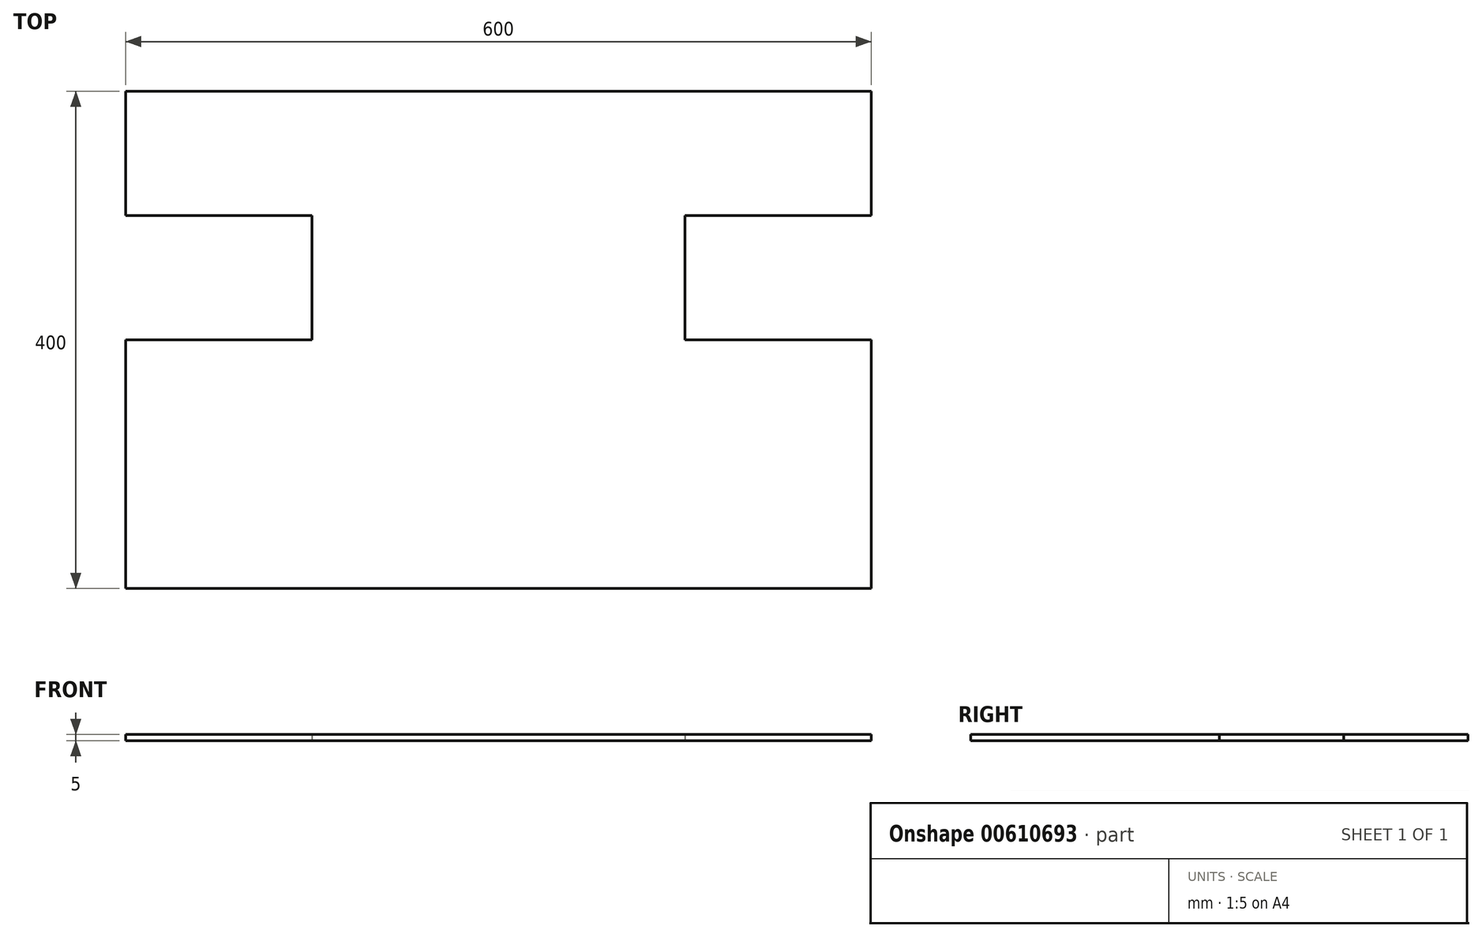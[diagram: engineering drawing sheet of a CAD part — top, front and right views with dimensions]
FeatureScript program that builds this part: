
annotation { "Feature Type Name" : "Feature", "Feature Type Description" : "" }
export const myFeature = defineFeature(function(context is Context, id is Id, definition is map)
    precondition{}
    {
        {
            var Q0;
            Q0=qCreatedBy(makeId("Top.planeOp"),FACE);
            var sketch = newSketch(context, id + "F0", { "sketchPlane" : qUnion([Q0])});
            skLineSegment(sketch, "E0.bottom", {"start": v(0, 0) * mm, "end": v(600, 0) * mm});
            skLineSegment(sketch, "E0.top", {"start": v(0, -400) * mm, "end": v(600, -400) * mm});
            skLineSegment(sketch, "E0.left", {"start": v(0, 0) * mm, "end": v(0, -400) * mm});
            skLineSegment(sketch, "E0.right", {"start": v(600, 0) * mm, "end": v(600, -400) * mm});
            skLineSegment(sketch, "E1.bottom", {"start": v(150, -400) * mm, "end": v(450, -400) * mm});
            skLineSegment(sketch, "E1.top", {"start": v(150, -570) * mm, "end": v(450, -570) * mm});
            skLineSegment(sketch, "E1.left", {"start": v(150, -400) * mm, "end": v(150, -570) * mm});
            skLineSegment(sketch, "E1.right", {"start": v(450, -400) * mm, "end": v(450, -570) * mm});
            skLineSegment(sketch, "E2.bottom", {"start": v(0, -100) * mm, "end": v(150, -100) * mm});
            skLineSegment(sketch, "E2.top", {"start": v(0, -200) * mm, "end": v(150, -200) * mm});
            skLineSegment(sketch, "E2.left", {"start": v(0, -100) * mm, "end": v(0, -200) * mm});
            skLineSegment(sketch, "E2.right", {"start": v(150, -100) * mm, "end": v(150, -200) * mm});
            skLineSegment(sketch, "E3.bottom", {"start": v(600, -100) * mm, "end": v(450, -100) * mm});
            skLineSegment(sketch, "E3.top", {"start": v(600, -200) * mm, "end": v(450, -200) * mm});
            skLineSegment(sketch, "E3.left", {"start": v(600, -100) * mm, "end": v(600, -200) * mm});
            skLineSegment(sketch, "E3.right", {"start": v(450, -100) * mm, "end": v(450, -200) * mm});
            skSolve(sketch);
        }
        {
            var Q0;
            {var subQ6=sQuery(id+"F0.wireOp",EDGE,"E0.bottom");Q0=makeQuery(id+"F0.imprint","IMPRINT",FACE,{"disambiguationData":[TD([[makeQuery(id+"F0.imprint","IMPRINT",EDGE,{"derivedFrom":subQ6}),-1.0]])]});}
            var Q1;
            Q1=makeQuery(id+"F0.imprint","IMPRINT",FACE,{"disambiguationData":[TD([[makeQuery(id+"F0.imprint","IMPRINT",EDGE,{"derivedFrom":sQuery(id+"F0.wireOp",EDGE,"E1.bottom")}),-1.0]])]});
            extrude(context, id + "F1", {"entities" : qUnion([Q0, Q1]), "depth" : 5 * mm, "offsetDistance" : 25 * mm});
        }
    });
